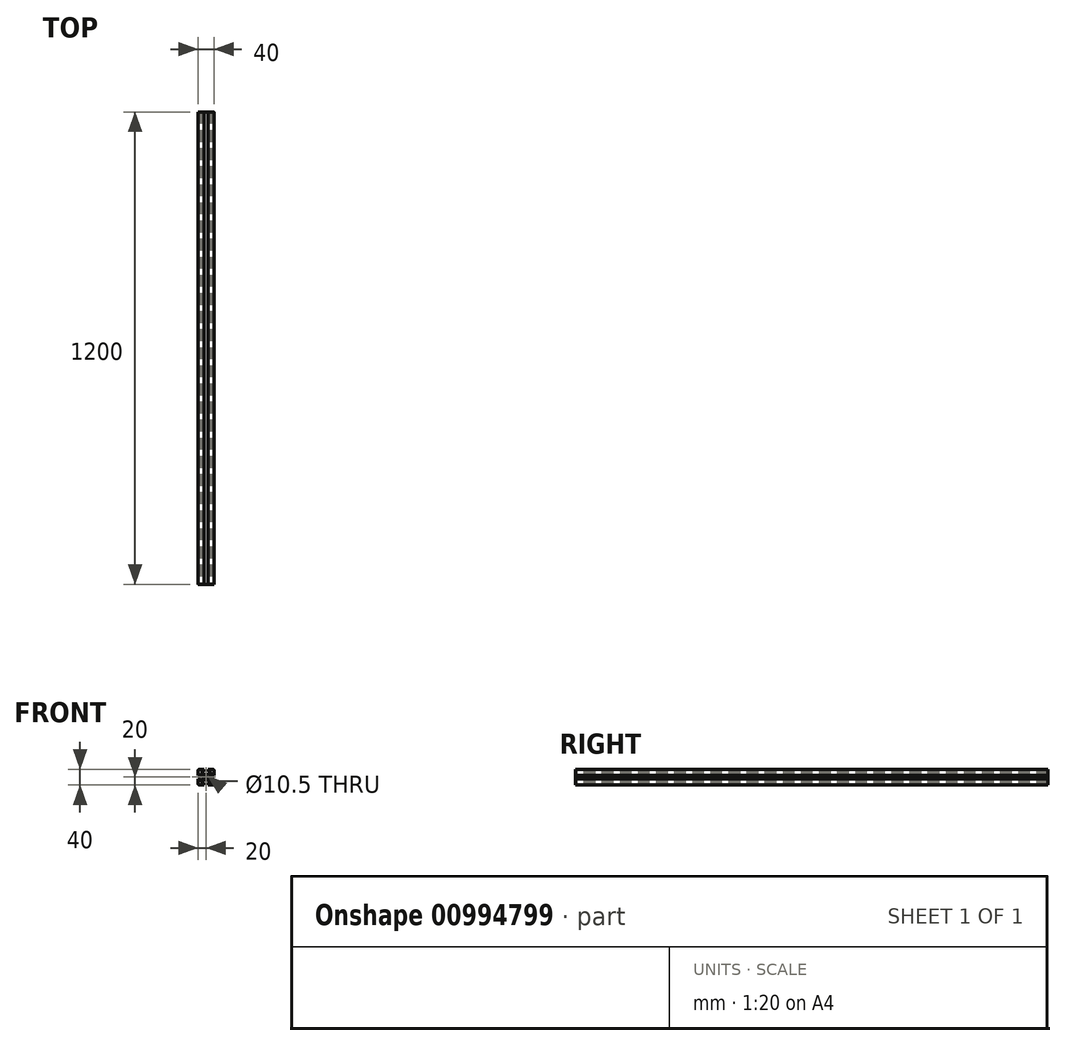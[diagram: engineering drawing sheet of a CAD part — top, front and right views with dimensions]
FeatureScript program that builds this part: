
annotation { "Feature Type Name" : "Feature", "Feature Type Description" : "" }
export const myFeature = defineFeature(function(context is Context, id is Id, definition is map)
    precondition{}
    {
        {
            var Q0;
            Q0=qCreatedBy(makeId("Front.planeOp"),FACE);
            var sketch = newSketch(context, id + "F0", { "sketchPlane" : qUnion([Q0])});
            skLineSegment(sketch, "E0", {"start": v(20, 20) * mm, "end": v(-20, 20) * mm});
            skLineSegment(sketch, "E1", {"start": v(-20, 20) * mm, "end": v(-20, -20) * mm});
            skLineSegment(sketch, "E2", {"start": v(-20, -20) * mm, "end": v(20, -20) * mm});
            skLineSegment(sketch, "E3", {"start": v(20, -20) * mm, "end": v(20, 20) * mm});
            skSolve(sketch);
        }
        {
            var Q0;
            Q0 = qSketchRegion(id + "F0", true);
            extrude(context, id + "F1", {"entities" : qUnion([Q0]), "oppositeDirection" : true, "depth" : 1200 * mm, "offsetDistance" : 25 * mm});
        }
        {
            var Q0;
            Q0=qCreatedBy(makeId("Front.planeOp"),FACE);
            var sketch = newSketch(context, id + "F2", { "sketchPlane" : qUnion([Q0])});
            skCircle(sketch, "E4", {"center": v(0, 0) * mm, "radius": 5.25 * mm});
            skSolve(sketch);
        }
        {
            var Q0;
            Q0 = qSketchRegion(id + "F2", true);
            extrude(context, id + "F3", {"entities" : qUnion([Q0]), "operationType" : NewBodyOperationType.REMOVE, "oppositeDirection" : true, "depth" : 1200 * mm, "offsetDistance" : 25 * mm});
        }
        {
            var Q0;
            Q0=qCreatedBy(makeId("Front.planeOp"),FACE);
            var sketch = newSketch(context, id + "F4", { "sketchPlane" : qUnion([Q0])});
            skLineSegment(sketch, "E5", {"start": v(10, 14.5) * mm, "end": v(5, 14.5) * mm});
            skLineSegment(sketch, "E6", {"start": v(14.5, 5) * mm, "end": v(20, 5) * mm});
            skLineSegment(sketch, "E7", {"start": v(5, 14.5) * mm, "end": v(10, 14.5) * mm});
            skLineSegment(sketch, "E8", {"start": v(10, 14.5) * mm, "end": v(10, 12.5) * mm});
            skLineSegment(sketch, "E9", {"start": v(20, 5) * mm, "end": v(14.5, 5) * mm});
            skLineSegment(sketch, "E10", {"start": v(5, 7.5) * mm, "end": v(10, 12.5) * mm});
            skLineSegment(sketch, "E11", {"start": v(7.5, 5) * mm, "end": v(12.5, 10) * mm});
            skLineSegment(sketch, "E12", {"start": v(12.5, 10) * mm, "end": v(14.5, 10) * mm});
            skLineSegment(sketch, "E13", {"start": v(14.5, 10) * mm, "end": v(14.5, 5) * mm});
            skLineSegment(sketch, "E14", {"start": v(5, 14.5) * mm, "end": v(5, 20) * mm});
            skLineSegment(sketch, "E15.1.1", {"start": v(5, -7.5) * mm, "end": v(10, -12.5) * mm});
            skLineSegment(sketch, "E15.1.2", {"start": v(14.5, -5) * mm, "end": v(20, -5) * mm});
            skLineSegment(sketch, "E15.1.3", {"start": v(10, -12.5) * mm, "end": v(10, -14.5) * mm});
            skLineSegment(sketch, "E15.1.4", {"start": v(5, -20) * mm, "end": v(5, -14.5) * mm});
            skLineSegment(sketch, "E15.1.5", {"start": v(10, -14.5) * mm, "end": v(5, -14.5) * mm});
            skLineSegment(sketch, "E15.1.7", {"start": v(14.5, -10) * mm, "end": v(14.5, -5) * mm});
            skLineSegment(sketch, "E15.1.8", {"start": v(7.5, -5) * mm, "end": v(12.5, -10) * mm});
            skLineSegment(sketch, "E15.1.12", {"start": v(14.5, -5) * mm, "end": v(14.5, -10) * mm});
            skLineSegment(sketch, "E15.1.15", {"start": v(5, -14.5) * mm, "end": v(5, -20) * mm});
            skLineSegment(sketch, "E15.1.16", {"start": v(14.5, -10) * mm, "end": v(12.5, -10) * mm});
            skLineSegment(sketch, "E15.2.1", {"start": v(-7.5, -5) * mm, "end": v(-12.5, -10) * mm});
            skLineSegment(sketch, "E15.2.2", {"start": v(-5, -14.5) * mm, "end": v(-5, -20) * mm});
            skLineSegment(sketch, "E15.2.3", {"start": v(-12.5, -10) * mm, "end": v(-14.5, -10) * mm});
            skLineSegment(sketch, "E15.2.4", {"start": v(-20, -5) * mm, "end": v(-14.5, -5) * mm});
            skLineSegment(sketch, "E15.2.5", {"start": v(-14.5, -10) * mm, "end": v(-14.5, -5) * mm});
            skLineSegment(sketch, "E15.2.7", {"start": v(-10, -14.5) * mm, "end": v(-5, -14.5) * mm});
            skLineSegment(sketch, "E15.2.8", {"start": v(-5, -7.5) * mm, "end": v(-10, -12.5) * mm});
            skLineSegment(sketch, "E15.2.12", {"start": v(-5, -14.5) * mm, "end": v(-10, -14.5) * mm});
            skLineSegment(sketch, "E15.2.15", {"start": v(-14.5, -5) * mm, "end": v(-20, -5) * mm});
            skLineSegment(sketch, "E15.2.16", {"start": v(-10, -14.5) * mm, "end": v(-10, -12.5) * mm});
            skPoint(sketch, "E15.center", {"position": v(0, 0) * mm});
            skLineSegment(sketch, "E16.1.0", {"start": v(-14.5, 5) * mm, "end": v(-14.5, 10) * mm});
            skLineSegment(sketch, "E16.1.1", {"start": v(-10, 14.5) * mm, "end": v(-5, 14.5) * mm});
            skLineSegment(sketch, "E16.1.2", {"start": v(-5, 7.5) * mm, "end": v(-10, 12.5) * mm});
            skLineSegment(sketch, "E16.1.3", {"start": v(-5, 20) * mm, "end": v(-5, 14.5) * mm});
            skLineSegment(sketch, "E16.1.5", {"start": v(-14.5, 5) * mm, "end": v(-20, 5) * mm});
            skLineSegment(sketch, "E16.1.7", {"start": v(-7.5, 5) * mm, "end": v(-12.5, 10) * mm});
            skLineSegment(sketch, "E16.1.10", {"start": v(-14.5, 10) * mm, "end": v(-14.5, 5) * mm});
            skLineSegment(sketch, "E16.1.11", {"start": v(-5, 14.5) * mm, "end": v(-5, 20) * mm});
            skLineSegment(sketch, "E16.1.16", {"start": v(-10, 12.5) * mm, "end": v(-10, 14.5) * mm});
            skLineSegment(sketch, "E16.1.18", {"start": v(-14.5, 10) * mm, "end": v(-12.5, 10) * mm});
            skLineSegment(sketch, "E17", {"start": v(-7.5, 5) * mm, "end": v(-7.5, -5) * mm});
            skLineSegment(sketch, "E18", {"start": v(-5, 7.5) * mm, "end": v(5, 7.5) * mm});
            skLineSegment(sketch, "E19", {"start": v(7.5, 5) * mm, "end": v(7.5, -5) * mm});
            skLineSegment(sketch, "E20", {"start": v(5, -7.5) * mm, "end": v(-5, -7.5) * mm});
            skLineSegment(sketch, "E21", {"start": v(-5, 20) * mm, "end": v(5, 20) * mm});
            skLineSegment(sketch, "E22", {"start": v(20, 5) * mm, "end": v(20, -5) * mm});
            skLineSegment(sketch, "E23", {"start": v(-20, 5) * mm, "end": v(-20, -5) * mm});
            skLineSegment(sketch, "E24", {"start": v(-5, -20) * mm, "end": v(5, -20) * mm});
            skSolve(sketch);
        }
        {
            var Q0;
            Q0 = qSketchRegion(id + "F4", true);
            extrude(context, id + "F5", {"entities" : qUnion([Q0]), "operationType" : NewBodyOperationType.REMOVE, "oppositeDirection" : true, "depth" : 1200 * mm, "offsetDistance" : 25 * mm});
        }
        {
            var Q0;
            Q0=makeQuery(id+"F1.opExtrude","SWEPT_EDGE",EDGE,{"disambiguationData":[OSD([sQuery(id+"F0.wireOp",EDGE,"E0"),sQuery(id+"F0.wireOp",EDGE,"E1")])]});
            var Q1;
            Q1=makeQuery(id+"F1.opExtrude","SWEPT_EDGE",EDGE,{"disambiguationData":[OSD([sQuery(id+"F0.wireOp",EDGE,"E0"),sQuery(id+"F0.wireOp",EDGE,"E3")])]});
            var Q2;
            Q2=makeQuery(id+"F1.opExtrude","SWEPT_EDGE",EDGE,{"disambiguationData":[OSD([sQuery(id+"F0.wireOp",EDGE,"E2"),sQuery(id+"F0.wireOp",EDGE,"E3")])]});
            var Q3;
            Q3=makeQuery(id+"F1.opExtrude","SWEPT_EDGE",EDGE,{"disambiguationData":[OSD([sQuery(id+"F0.wireOp",EDGE,"E1"),sQuery(id+"F0.wireOp",EDGE,"E2")])]});
            fillet(context, id + "F6", {"entities" : qUnion([Q0, Q1, Q2, Q3]), "tangentPropagation" : true, "radius" : 3 * mm, "defaultsChanged" : false, "vertexSettings" : [], "allowEdgeOverflow" : false});
        }
        {
            var Q0;
            Q0=makeQuery(id+"F5.boolean.opBoolean","COPY",EDGE,{"derivedFrom":makeQuery(id+"F5.opExtrude","SWEPT_EDGE",EDGE,{"disambiguationData":[OSD([sQuery(id+"F4.wireOp",EDGE,"E16.1.11"),sQuery(id+"F4.wireOp",EDGE,"E21")])]})});
            var Q1;
            Q1=makeQuery(id+"F5.boolean.opBoolean","COPY",EDGE,{"derivedFrom":makeQuery(id+"F5.opExtrude","SWEPT_EDGE",EDGE,{"disambiguationData":[OSD([sQuery(id+"F4.wireOp",EDGE,"E16.1.1"),sQuery(id+"F4.wireOp",EDGE,"E16.1.11")])]})});
            var Q2;
            Q2=makeQuery(id+"F5.boolean.opBoolean","COPY",EDGE,{"derivedFrom":makeQuery(id+"F5.opExtrude","SWEPT_EDGE",EDGE,{"disambiguationData":[OSD([sQuery(id+"F4.wireOp",EDGE,"E14"),sQuery(id+"F4.wireOp",EDGE,"E21")])]})});
            var Q3;
            Q3=makeQuery(id+"F5.boolean.opBoolean","COPY",EDGE,{"derivedFrom":makeQuery(id+"F5.opExtrude","SWEPT_EDGE",EDGE,{"disambiguationData":[OSD([sQuery(id+"F4.wireOp",EDGE,"E9"),sQuery(id+"F4.wireOp",EDGE,"E22")])]})});
            var Q4;
            Q4=makeQuery(id+"F5.boolean.opBoolean","COPY",EDGE,{"derivedFrom":makeQuery(id+"F5.opExtrude","SWEPT_EDGE",EDGE,{"disambiguationData":[OSD([sQuery(id+"F4.wireOp",EDGE,"E15.1.2"),sQuery(id+"F4.wireOp",EDGE,"E15.1.12")])]})});
            var Q5;
            Q5=makeQuery(id+"F5.boolean.opBoolean","COPY",EDGE,{"derivedFrom":makeQuery(id+"F5.opExtrude","SWEPT_EDGE",EDGE,{"disambiguationData":[OSD([sQuery(id+"F4.wireOp",EDGE,"E15.1.2"),sQuery(id+"F4.wireOp",EDGE,"E22")])]})});
            var Q6;
            Q6=makeQuery(id+"F5.boolean.opBoolean","COPY",EDGE,{"derivedFrom":makeQuery(id+"F5.opExtrude","SWEPT_EDGE",EDGE,{"disambiguationData":[OSD([sQuery(id+"F4.wireOp",EDGE,"E15.1.5"),sQuery(id+"F4.wireOp",EDGE,"E15.1.15")])]})});
            var Q7;
            Q7=makeQuery(id+"F5.boolean.opBoolean","COPY",EDGE,{"derivedFrom":makeQuery(id+"F5.opExtrude","SWEPT_EDGE",EDGE,{"disambiguationData":[OSD([sQuery(id+"F4.wireOp",EDGE,"E15.2.2"),sQuery(id+"F4.wireOp",EDGE,"E15.2.12")])]})});
            var Q8;
            Q8=makeQuery(id+"F5.boolean.opBoolean","COPY",EDGE,{"derivedFrom":makeQuery(id+"F5.opExtrude","SWEPT_EDGE",EDGE,{"disambiguationData":[OSD([sQuery(id+"F4.wireOp",EDGE,"E15.2.2"),sQuery(id+"F4.wireOp",EDGE,"E24")])]})});
            var Q9;
            Q9=makeQuery(id+"F5.boolean.opBoolean","COPY",EDGE,{"derivedFrom":makeQuery(id+"F5.opExtrude","SWEPT_EDGE",EDGE,{"disambiguationData":[OSD([sQuery(id+"F4.wireOp",EDGE,"E15.2.15"),sQuery(id+"F4.wireOp",EDGE,"E23")])]})});
            var Q10;
            Q10=makeQuery(id+"F5.boolean.opBoolean","COPY",EDGE,{"derivedFrom":makeQuery(id+"F5.opExtrude","SWEPT_EDGE",EDGE,{"disambiguationData":[OSD([sQuery(id+"F4.wireOp",EDGE,"E15.2.5"),sQuery(id+"F4.wireOp",EDGE,"E15.2.15")])]})});
            var Q11;
            Q11=makeQuery(id+"F5.boolean.opBoolean","COPY",EDGE,{"derivedFrom":makeQuery(id+"F5.opExtrude","SWEPT_EDGE",EDGE,{"disambiguationData":[OSD([sQuery(id+"F4.wireOp",EDGE,"E16.1.5"),sQuery(id+"F4.wireOp",EDGE,"E16.1.10")])]})});
            var Q12;
            Q12=makeQuery(id+"F5.boolean.opBoolean","COPY",EDGE,{"derivedFrom":makeQuery(id+"F5.opExtrude","SWEPT_EDGE",EDGE,{"disambiguationData":[OSD([sQuery(id+"F4.wireOp",EDGE,"E15.1.15"),sQuery(id+"F4.wireOp",EDGE,"E24")])]})});
            var Q13;
            Q13=makeQuery(id+"F5.boolean.opBoolean","COPY",EDGE,{"derivedFrom":makeQuery(id+"F5.opExtrude","SWEPT_EDGE",EDGE,{"disambiguationData":[OSD([sQuery(id+"F4.wireOp",EDGE,"E9"),sQuery(id+"F4.wireOp",EDGE,"E13")])]})});
            var Q14;
            Q14=makeQuery(id+"F5.boolean.opBoolean","COPY",EDGE,{"derivedFrom":makeQuery(id+"F5.opExtrude","SWEPT_EDGE",EDGE,{"disambiguationData":[OSD([sQuery(id+"F4.wireOp",EDGE,"E7"),sQuery(id+"F4.wireOp",EDGE,"E14")])]})});
            var Q15;
            Q15=makeQuery(id+"F5.boolean.opBoolean","COPY",EDGE,{"derivedFrom":makeQuery(id+"F5.opExtrude","SWEPT_EDGE",EDGE,{"disambiguationData":[OSD([sQuery(id+"F4.wireOp",EDGE,"E16.1.5"),sQuery(id+"F4.wireOp",EDGE,"E23")])]})});
            fillet(context, id + "F7", {"entities" : qUnion([Q0, Q1, Q2, Q3, Q4, Q5, Q6, Q7, Q8, Q9, Q10, Q11, Q12, Q13, Q14, Q15]), "tangentPropagation" : true, "radius" : 1 * mm, "defaultsChanged" : false, "vertexSettings" : [], "allowEdgeOverflow" : false});
        }
    });
